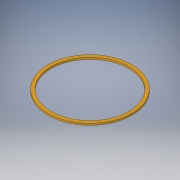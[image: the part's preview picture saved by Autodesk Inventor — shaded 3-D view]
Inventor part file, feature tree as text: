
AUTODESK INVENTOR PART (.ipt)
format: ipt  version: 2019 (Build 230136000, 136)  size: 103,424 bytes
history: native  units: mm
features: extrude x1, sketch x1
ambient origin geometry x8: Origin, YZ Plane, XZ Plane, XY Plane, X Axis, Y Axis, Z Axis, Center Point
bodies: Solid1 (feature_tree)
feature tree (2):
  extrude  "Extrusion1"  [1 undecoded]
  sketch  "Sketch1"  dims[d2=100.0mm d3=0.0mm]
note: 1 required parameter value undecoded (feature->parameter linkage not recoverable at this tier; creation-order binding heuristic only, values carry confidence <= 0.55)
